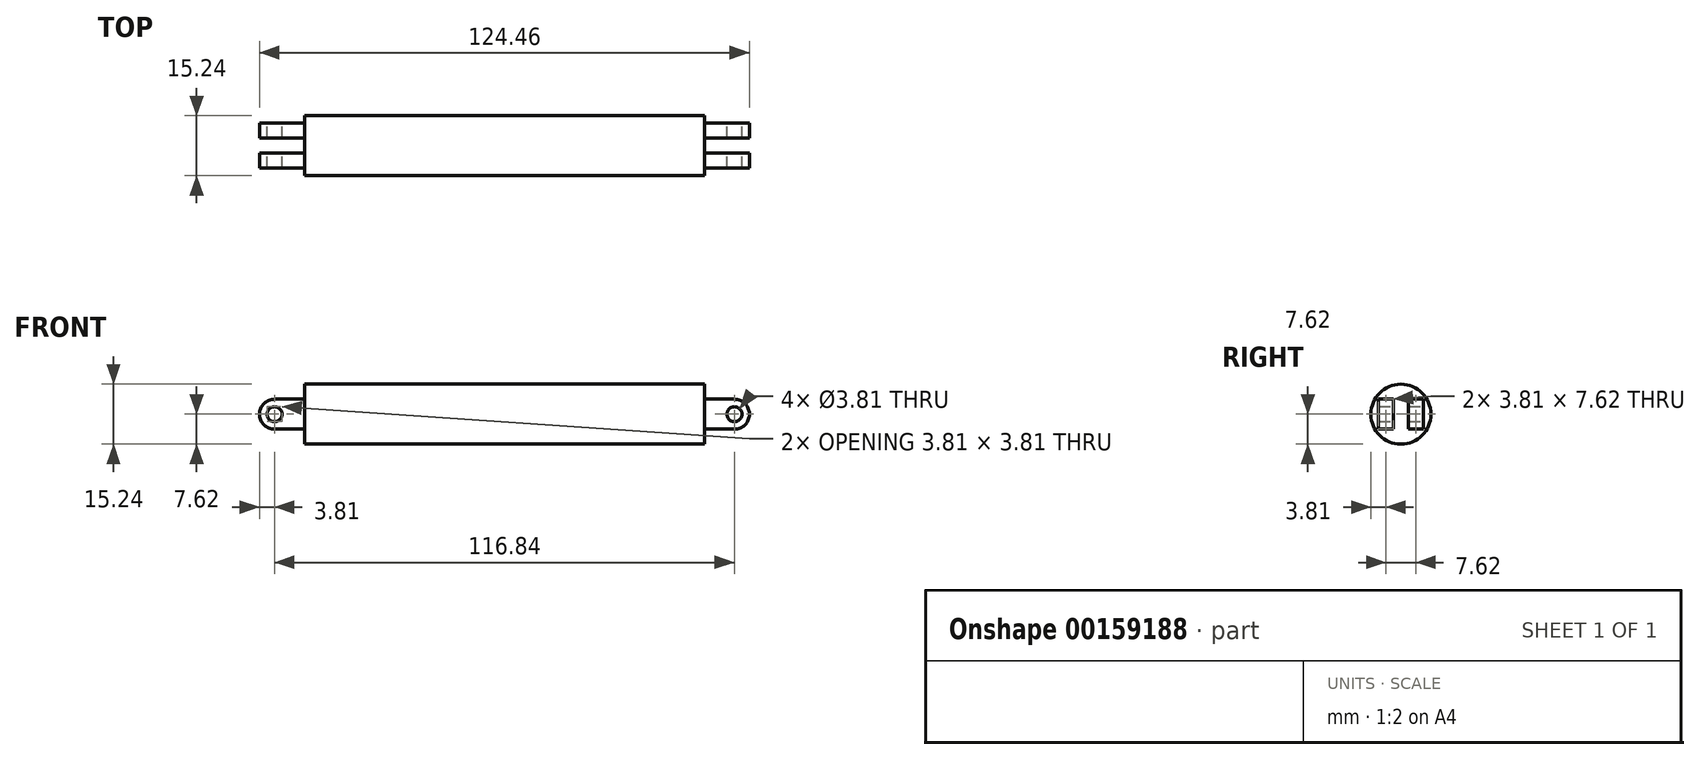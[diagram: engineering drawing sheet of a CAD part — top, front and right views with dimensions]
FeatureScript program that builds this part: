
annotation { "Feature Type Name" : "Feature", "Feature Type Description" : "" }
export const myFeature = defineFeature(function(context is Context, id is Id, definition is map)
    precondition{}
    {
        {
            var Q0;
            Q0=qCreatedBy(makeId("Right.planeOp"),FACE);
            var sketch = newSketch(context, id + "F0", { "sketchPlane" : qUnion([Q0])});
            skCircle(sketch, "E0", {"center": v(0, 0) * mm, "radius": 7.62 * mm});
            skSolve(sketch);
        }
        {
            var Q0;
            Q0=makeQuery(id+"F0.imprint","IMPRINT",FACE,{"disambiguationData":[TD([[makeQuery(id+"F0.imprint","IMPRINT",EDGE,{"derivedFrom":sQuery(id+"F0.wireOp",EDGE,"E0")}),1.0]])]});
            extrude(context, id + "F1", {"entities" : qUnion([Q0]), "endBound" : BoundingType.SYMMETRIC, "depth" : 101.6 * mm});
        }
        {
            var Q0;
            Q0=qCreatedBy(makeId("Front.planeOp"),FACE);
            var sketch = newSketch(context, id + "F2", { "sketchPlane" : qUnion([Q0])});
            skLineSegment(sketch, "E1", {"start": v(50.8, 0) * mm, "end": v(66.48, 0) * mm, "construction": true});
            skLineSegment(sketch, "E2", {"start": v(50.8, 0) * mm, "end": v(50.8, 3.81) * mm});
            skLineSegment(sketch, "E3", {"start": v(50.8, 0) * mm, "end": v(50.8, -3.8) * mm});
            skLineSegment(sketch, "E4.bottom", {"start": v(50.8, 3.81) * mm, "end": v(58.42, 3.81) * mm});
            skLineSegment(sketch, "E4.top", {"start": v(50.8, -3.8) * mm, "end": v(58.42, -3.8) * mm});
            skLineSegment(sketch, "E4.left", {"start": v(50.8, 3.81) * mm, "end": v(50.8, -3.8) * mm});
            skArc(sketch, "E5", {"start": v(58.42, -3.8) * mm, "mid": v(62.23, 0) * mm, "end": v(58.42, 3.81) * mm});
            skCircle(sketch, "E6", {"center": v(58.42, 0) * mm, "radius": 1.9 * mm});
            skSolve(sketch);
        }
        {
            var Q0;
            {var subQ1=sQuery(id+"F2.wireOp",EDGE,"E4.bottom");Q0=makeQuery(id+"F2.imprint","IMPRINT",FACE,{"disambiguationData":[TD([[makeQuery(id+"F2.imprint","IMPRINT",EDGE,{"derivedFrom":subQ1}),-1.0]])]});}
            extrude(context, id + "F3", {"entities" : qUnion([Q0]), "operationType" : NewBodyOperationType.ADD, "endBound" : BoundingType.SYMMETRIC, "depth" : 11.43 * mm});
        }
        {
            var Q0;
            Q0=makeQuery(id+"F1.opExtrude","CAP_FACE",FACE,{"disambiguationData":[OSD([sQuery(id+"F0.wireOp",EDGE,"E0")])],"isStart":false});
            var sketch = newSketch(context, id + "F4", { "sketchPlane" : qUnion([Q0])});
            skLineSegment(sketch, "E7.bottom", {"start": v(-1.9, 3.81) * mm, "end": v(1.9, 3.81) * mm});
            skLineSegment(sketch, "E7.top", {"start": v(-1.9, -3.8) * mm, "end": v(1.9, -3.8) * mm});
            skLineSegment(sketch, "E7.left", {"start": v(-1.9, 3.81) * mm, "end": v(-1.9, -3.8) * mm});
            skLineSegment(sketch, "E7.right", {"start": v(1.9, 3.81) * mm, "end": v(1.9, -3.81) * mm});
            skPoint(sketch, "E7.middle", {"position": v(0, 0) * mm});
            skSolve(sketch);
        }
        {
            var Q0;
            Q0 = qSketchRegion(id + "F4", true);
            extrude(context, id + "F5", {"entities" : qUnion([Q0]), "operationType" : NewBodyOperationType.REMOVE, "endBound" : BoundingType.THROUGH_ALL, "depth" : 25.4 * mm});
        }
        {
            var Q0;
            Q0=makeQuery(id+"F1.opExtrude","SWEPT_BODY",BODY,{"disambiguationData":[OSD([sQuery(id+"F0.wireOp",EDGE,"E0")])]});
            var Q1;
            Q1=qCreatedBy(makeId("Right.planeOp"),FACE);
            mirror(context, id + "F6", {"operationType" : NewBodyOperationType.ADD, "entities" : qUnion([Q0]), "mirrorPlane" : qUnion([Q1])});
        }
    });
